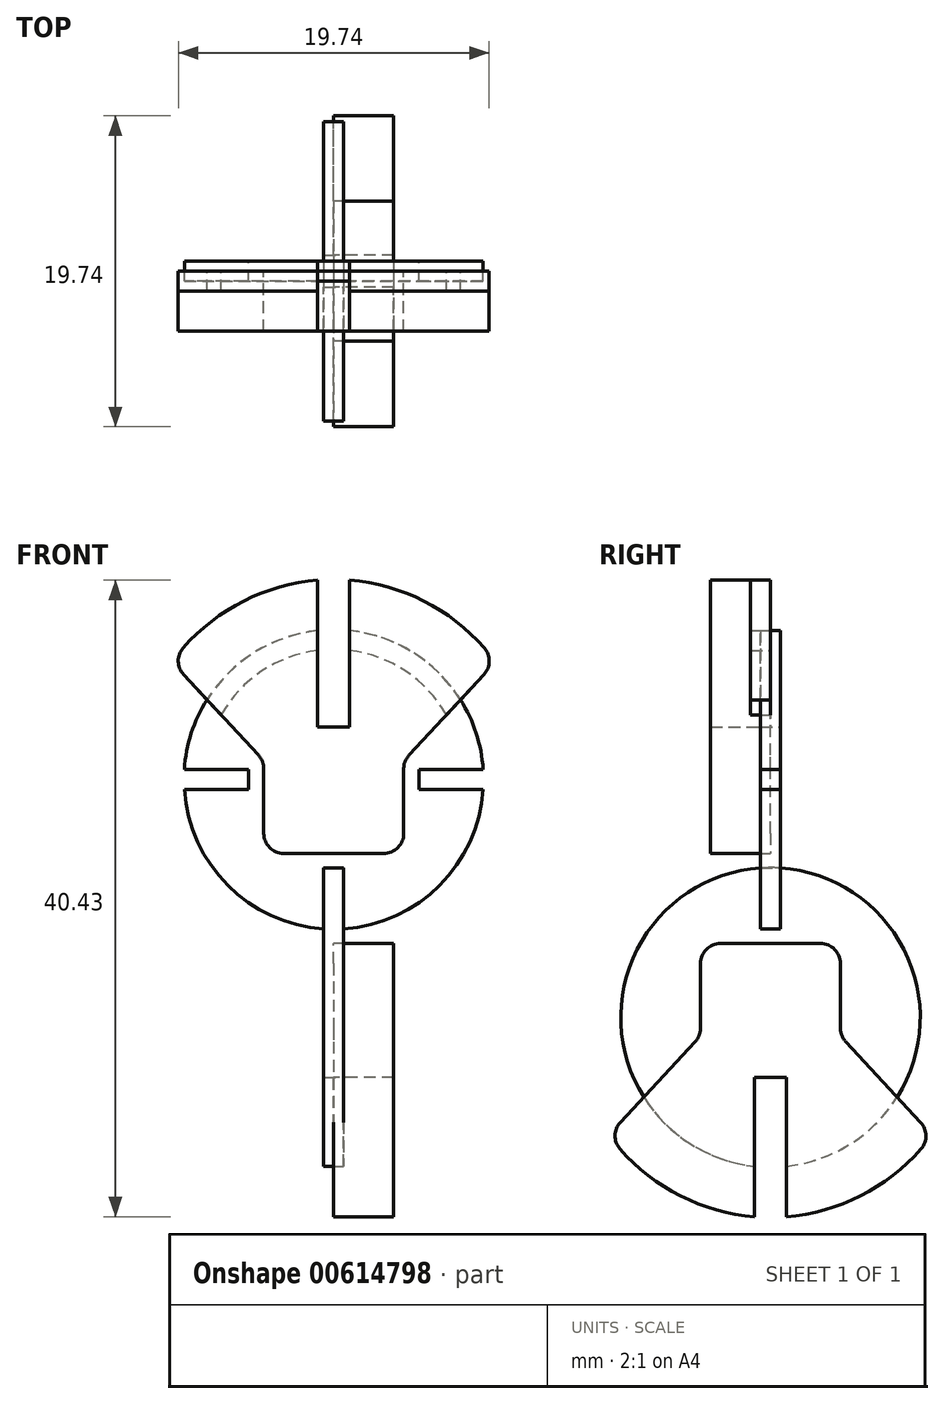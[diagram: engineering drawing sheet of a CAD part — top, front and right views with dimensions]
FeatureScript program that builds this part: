
annotation { "Feature Type Name" : "Feature", "Feature Type Description" : "" }
export const myFeature = defineFeature(function(context is Context, id is Id, definition is map)
    precondition{}
    {
        {
            var Q0;
            Q0=qCreatedBy(makeId("Front.planeOp"),FACE);
            var sketch = newSketch(context, id + "F0", { "sketchPlane" : qUnion([Q0])});
            skArc(sketch, "E0", {"start": v(-1.02, 9.46) * mm, "mid": v(0, -9.51) * mm, "end": v(1.02, 9.46) * mm});
            skLineSegment(sketch, "E1.bottom", {"start": v(0.63, -24.51) * mm, "end": v(-0.63, -24.51) * mm});
            skLineSegment(sketch, "E1.top", {"start": v(0.63, 24.51) * mm, "end": v(-0.63, 24.51) * mm});
            skLineSegment(sketch, "E1.left", {"start": v(0.64, -24.51) * mm, "end": v(0.64, -5.62) * mm});
            skLineSegment(sketch, "E1.right", {"start": v(-0.63, -24.51) * mm, "end": v(-0.63, -5.62) * mm});
            skLineSegment(sketch, "E2.bottom", {"start": v(0.64, 5.62) * mm, "end": v(-0.64, 5.62) * mm});
            skLineSegment(sketch, "E2.top", {"start": v(0.64, -5.62) * mm, "end": v(-0.64, -5.62) * mm});
            skLineSegment(sketch, "E3.trimOffspring", {"start": v(0.64, 5.62) * mm, "end": v(0.64, 24.51) * mm});
            skLineSegment(sketch, "E4.trimOffspring", {"start": v(-0.63, 5.62) * mm, "end": v(-0.63, 24.51) * mm});
            skPoint(sketch, "E5", {"position": v(0, 5.62) * mm});
            skLineSegment(sketch, "E6", {"start": v(-1.02, 9.46) * mm, "end": v(-1.02, 3.34) * mm});
            skLineSegment(sketch, "E7", {"start": v(1.02, 9.46) * mm, "end": v(1.02, 3.34) * mm});
            skLineSegment(sketch, "E8", {"start": v(-1.02, 3.34) * mm, "end": v(1.02, 3.34) * mm});
            skLineSegment(sketch, "E9", {"start": v(-1.02, 9.46) * mm, "end": v(-1.02, 12.66) * mm});
            skLineSegment(sketch, "E10", {"start": v(1.02, 9.46) * mm, "end": v(1.02, 12.66) * mm});
            skLineSegment(sketch, "E11.bottom", {"start": v(-5.43, -0.64) * mm, "end": v(-9.49, -0.64) * mm});
            skLineSegment(sketch, "E11.top", {"start": v(-5.43, 0.63) * mm, "end": v(-9.49, 0.63) * mm});
            skLineSegment(sketch, "E11.left", {"start": v(-5.43, -0.64) * mm, "end": v(-5.43, 0.63) * mm});
            skLineSegment(sketch, "E11.right", {"start": v(-9.49, -0.64) * mm, "end": v(-9.49, 0.63) * mm});
            skPoint(sketch, "E11.middle", {"position": v(-7.46, 0) * mm});
            skLineSegment(sketch, "E12", {"start": v(-3.18, -4.7) * mm, "end": v(3.18, -4.7) * mm});
            skLineSegment(sketch, "E13.MirrorCS", {"start": v(5.43, 0.63) * mm, "end": v(9.49, 0.63) * mm});
            skLineSegment(sketch, "E14.MirrorCS", {"start": v(5.43, -0.64) * mm, "end": v(9.49, -0.64) * mm});
            skLineSegment(sketch, "E15.MirrorCS", {"start": v(5.43, -0.64) * mm, "end": v(5.43, 0.63) * mm});
            skLineSegment(sketch, "E16", {"start": v(4.44, -3.42) * mm, "end": v(4.44, 0.68) * mm});
            skPoint(sketch, "E16.endSnap0", {"position": v(-7.46, 0.63) * mm});
            skLineSegment(sketch, "E17", {"start": v(4.78, 1.55) * mm, "end": v(9.53, 6.66) * mm});
            skLineSegment(sketch, "E18.MirrorCS", {"start": v(-4.44, -3.42) * mm, "end": v(-4.44, 0.68) * mm});
            skLineSegment(sketch, "E19.MirrorCS", {"start": v(-4.78, 1.55) * mm, "end": v(-9.53, 6.66) * mm});
            skArc(sketch, "E20.trimOffspring", {"start": v(7.16, 4.1) * mm, "mid": v(4.57, 6.87) * mm, "end": v(1.02, 8.2) * mm});
            skArc(sketch, "E21.trimOffspring", {"start": v(9.56, 8.36) * mm, "mid": v(5.7, 11.34) * mm, "end": v(1.02, 12.66) * mm});
            skArc(sketch, "E22.trimOffspring", {"start": v(-0.63, -8.23) * mm, "mid": v(0, -8.26) * mm, "end": v(0.64, -8.23) * mm});
            skArc(sketch, "E23.trimOffspring", {"start": v(-1.02, 8.2) * mm, "mid": v(-4.57, 6.87) * mm, "end": v(-7.16, 4.1) * mm});
            skPoint(sketch, "E24.visualSharp", {"position": v(-10.28, 7.46) * mm});
            skArc(sketch, "E24.filletArc", {"start": v(-9.56, 8.36) * mm, "mid": v(-9.87, 7.5) * mm, "end": v(-9.53, 6.66) * mm});
            skPoint(sketch, "E25.visualSharp", {"position": v(10.28, 7.46) * mm});
            skArc(sketch, "E25.filletArc", {"start": v(9.53, 6.66) * mm, "mid": v(9.87, 7.5) * mm, "end": v(9.56, 8.36) * mm});
            skPoint(sketch, "E26.visualSharp", {"position": v(4.44, 1.18) * mm});
            skArc(sketch, "E26.filletArc", {"start": v(4.78, 1.55) * mm, "mid": v(4.53, 1.15) * mm, "end": v(4.44, 0.68) * mm});
            skPoint(sketch, "E27.visualSharp", {"position": v(-4.44, 1.18) * mm});
            skArc(sketch, "E27.filletArc", {"start": v(-4.44, 0.68) * mm, "mid": v(-4.53, 1.15) * mm, "end": v(-4.78, 1.55) * mm});
            skPoint(sketch, "E28.visualSharp", {"position": v(-4.44, -4.7) * mm});
            skArc(sketch, "E28.filletArc", {"start": v(-4.44, -3.42) * mm, "mid": v(-4.07, -4.32) * mm, "end": v(-3.18, -4.7) * mm});
            skPoint(sketch, "E29.visualSharp", {"position": v(4.44, -4.7) * mm});
            skArc(sketch, "E29.filletArc", {"start": v(3.18, -4.7) * mm, "mid": v(4.07, -4.32) * mm, "end": v(4.44, -3.42) * mm});
            skArc(sketch, "E30.trimOffspring", {"start": v(-1.02, 12.66) * mm, "mid": v(-5.7, 11.34) * mm, "end": v(-9.56, 8.36) * mm});
            skSolve(sketch);
        }
        {
            var Q0;
            {var subQ6=sQuery(id+"F0.wireOp",EDGE,"E8");Q0=makeQuery(id+"F0.imprint","IMPRINT",FACE,{"disambiguationData":[TD([[makeQuery(id+"F0.imprint","IMPRINT",EDGE,{"derivedFrom":subQ6}),-1.0]])]});}
            var Q1;
            {var subQ5=sQuery(id+"F0.wireOp",EDGE,"E20.trimOffspring");Q1=makeQuery(id+"F0.imprint","IMPRINT",FACE,{"disambiguationData":[TD([[makeQuery(id+"F0.imprint","IMPRINT",EDGE,{"derivedFrom":subQ5}),-1.0]])]});}
            var Q2;
            {var subQ1=sQuery(id+"F0.wireOp",EDGE,"E10");Q2=makeQuery(id+"F0.imprint","IMPRINT",FACE,{"disambiguationData":[TD([[makeQuery(id+"F0.imprint","IMPRINT",EDGE,{"derivedFrom":subQ1}),-1.0]])]});}
            var Q3;
            {var subQ5=sQuery(id+"F0.wireOp",EDGE,"E23.trimOffspring");Q3=makeQuery(id+"F0.imprint","IMPRINT",FACE,{"disambiguationData":[TD([[makeQuery(id+"F0.imprint","IMPRINT",EDGE,{"derivedFrom":subQ5}),-1.0]])]});}
            var Q4;
            {var subQ1=sQuery(id+"F0.wireOp",EDGE,"E9");Q4=makeQuery(id+"F0.imprint","IMPRINT",FACE,{"disambiguationData":[TD([[makeQuery(id+"F0.imprint","IMPRINT",EDGE,{"derivedFrom":subQ1}),1.0]])]});}
            extrude(context, id + "F1", {"entities" : qUnion([Q0, Q1, Q2, Q3, Q4]), "depth" : 3.8 * mm, "offsetDistance" : 25.4 * mm});
        }
        {
            var Q0;
            {var subQ1=sQuery(id+"F0.wireOp",EDGE,"E9");Q0=makeQuery(id+"F0.imprint","IMPRINT",FACE,{"disambiguationData":[TD([[makeQuery(id+"F0.imprint","IMPRINT",EDGE,{"derivedFrom":subQ1}),1.0]])]});}
            var Q1;
            {var subQ5=sQuery(id+"F0.wireOp",EDGE,"E23.trimOffspring");Q1=makeQuery(id+"F0.imprint","IMPRINT",FACE,{"disambiguationData":[TD([[makeQuery(id+"F0.imprint","IMPRINT",EDGE,{"derivedFrom":subQ5}),-1.0]])]});}
            var Q2;
            {var subQ1=sQuery(id+"F0.wireOp",EDGE,"E10");Q2=makeQuery(id+"F0.imprint","IMPRINT",FACE,{"disambiguationData":[TD([[makeQuery(id+"F0.imprint","IMPRINT",EDGE,{"derivedFrom":subQ1}),-1.0]])]});}
            var Q3;
            {var subQ5=sQuery(id+"F0.wireOp",EDGE,"E20.trimOffspring");Q3=makeQuery(id+"F0.imprint","IMPRINT",FACE,{"disambiguationData":[TD([[makeQuery(id+"F0.imprint","IMPRINT",EDGE,{"derivedFrom":subQ5}),-1.0]])]});}
            extrude(context, id + "F2", {"entities" : qUnion([Q0, Q1, Q2, Q3]), "depth" : 3.17 * mm, "offsetDistance" : 25.4 * mm});
        }
        {
            var Q0;
            {var subQ4=sQuery(id+"F0.wireOp",EDGE,"E10");Q0=makeQuery(id+"F0.imprint","IMPRINT",FACE,{"disambiguationData":[TD([[makeQuery(id+"F0.imprint","IMPRINT",EDGE,{"derivedFrom":subQ4}),-1.0]])]});}
            var Q1;
            {var subQ1=sQuery(id+"F0.wireOp",EDGE,"E9");Q1=makeQuery(id+"F0.imprint","IMPRINT",FACE,{"disambiguationData":[TD([[makeQuery(id+"F0.imprint","IMPRINT",EDGE,{"derivedFrom":subQ1}),1.0]])]});}
            extrude(context, id + "F3", {"entities" : qUnion([Q0, Q1]), "depth" : 1.27 * mm, "offsetDistance" : 25.4 * mm});
        }
        {
            var Q0;
            Q0=makeQuery(id+"F2.opExtrude","SWEPT_BODY",BODY,{"disambiguationData":[OSD([sQuery(id+"F0.wireOp",EDGE,"E6"),sQuery(id+"F0.wireOp",EDGE,"E9"),sQuery(id+"F0.wireOp",EDGE,"E19.MirrorCS"),sQuery(id+"F0.wireOp",EDGE,"E23.trimOffspring"),sQuery(id+"F0.wireOp",EDGE,"E24.filletArc"),sQuery(id+"F0.wireOp",EDGE,"E30.trimOffspring")])]});
            var Q1;
            Q1=makeQuery(id+"F2.opExtrude","SWEPT_BODY",BODY,{"disambiguationData":[OSD([sQuery(id+"F0.wireOp",EDGE,"E7"),sQuery(id+"F0.wireOp",EDGE,"E10"),sQuery(id+"F0.wireOp",EDGE,"E17"),sQuery(id+"F0.wireOp",EDGE,"E20.trimOffspring"),sQuery(id+"F0.wireOp",EDGE,"E21.trimOffspring"),sQuery(id+"F0.wireOp",EDGE,"E25.filletArc")])]});
            deleteBodies(context, id + "F4", {"entities" : qUnion([Q0, Q1])});
        }
        {
            var Q0;
            {var subQ1=sQuery(id+"F0.wireOp",EDGE,"E9");Q0=makeQuery(id+"F0.imprint","IMPRINT",FACE,{"disambiguationData":[TD([[makeQuery(id+"F0.imprint","IMPRINT",EDGE,{"derivedFrom":subQ1}),1.0]])]});}
            var Q1;
            {var subQ5=sQuery(id+"F0.wireOp",EDGE,"E23.trimOffspring");Q1=makeQuery(id+"F0.imprint","IMPRINT",FACE,{"disambiguationData":[TD([[makeQuery(id+"F0.imprint","IMPRINT",EDGE,{"derivedFrom":subQ5}),-1.0]])]});}
            var Q2;
            {var subQ5=sQuery(id+"F0.wireOp",EDGE,"E20.trimOffspring");Q2=makeQuery(id+"F0.imprint","IMPRINT",FACE,{"disambiguationData":[TD([[makeQuery(id+"F0.imprint","IMPRINT",EDGE,{"derivedFrom":subQ5}),-1.0]])]});}
            var Q3;
            {var subQ4=sQuery(id+"F0.wireOp",EDGE,"E10");Q3=makeQuery(id+"F0.imprint","IMPRINT",FACE,{"disambiguationData":[TD([[makeQuery(id+"F0.imprint","IMPRINT",EDGE,{"derivedFrom":subQ4}),-1.0]])]});}
            extrude(context, id + "F5", {"entities" : qUnion([Q0, Q1, Q2, Q3]), "depth" : 1.27 * mm, "offsetDistance" : 25.4 * mm});
        }
        {
            var Q0;
            {var subQ5=sQuery(id+"F0.wireOp",EDGE,"E20.trimOffspring");Q0=makeQuery(id+"F0.imprint","IMPRINT",FACE,{"disambiguationData":[TD([[makeQuery(id+"F0.imprint","IMPRINT",EDGE,{"derivedFrom":subQ5}),-1.0]])]});}
            var Q1;
            {var subQ5=sQuery(id+"F0.wireOp",EDGE,"E23.trimOffspring");Q1=makeQuery(id+"F0.imprint","IMPRINT",FACE,{"disambiguationData":[TD([[makeQuery(id+"F0.imprint","IMPRINT",EDGE,{"derivedFrom":subQ5}),-1.0]])]});}
            var Q2;
            {var subQ6=sQuery(id+"F0.wireOp",EDGE,"E8");Q2=makeQuery(id+"F0.imprint","IMPRINT",FACE,{"disambiguationData":[TD([[makeQuery(id+"F0.imprint","IMPRINT",EDGE,{"derivedFrom":subQ6}),-1.0]])]});}
            var Q3;
            {var subQ12=sQuery(id+"F0.wireOp",EDGE,"E2.top");Q3=makeQuery(id+"F0.imprint","IMPRINT",FACE,{"disambiguationData":[TD([[makeQuery(id+"F0.imprint","IMPRINT",EDGE,{"derivedFrom":subQ12}),-1.0]])]});}
            extrude(context, id + "F6", {"entities" : qUnion([Q0, Q1, Q2, Q3]), "endBound" : BoundingType.SYMMETRIC, "depth" : 1.27 * mm, "offsetDistance" : 25.4 * mm});
        }
        {
            var Q0;
            Q0=qCreatedBy(makeId("Right.planeOp"),FACE);
            var sketch = newSketch(context, id + "F7", { "sketchPlane" : qUnion([Q0])});
            skArc(sketch, "E31", {"start": v(1.02, -24.57) * mm, "mid": v(0, -5.6) * mm, "end": v(-1.02, -24.57) * mm});
            skLineSegment(sketch, "E32.top", {"start": v(-0.64, -9.49) * mm, "end": v(0.64, -9.49) * mm});
            skLineSegment(sketch, "E33", {"start": v(1.02, -24.57) * mm, "end": v(1.02, -18.92) * mm});
            skLineSegment(sketch, "E34", {"start": v(-1.02, -24.57) * mm, "end": v(-1.02, -18.92) * mm});
            skLineSegment(sketch, "E35", {"start": v(1.02, -18.92) * mm, "end": v(-1.02, -18.92) * mm});
            skLineSegment(sketch, "E36", {"start": v(1.02, -24.57) * mm, "end": v(1.02, -27.77) * mm});
            skLineSegment(sketch, "E37", {"start": v(-1.02, -24.57) * mm, "end": v(-1.02, -27.77) * mm});
            skLineSegment(sketch, "E38", {"start": v(3.17, -10.42) * mm, "end": v(-3.18, -10.42) * mm});
            skLineSegment(sketch, "E39", {"start": v(-4.45, -11.69) * mm, "end": v(-4.45, -15.8) * mm});
            skLineSegment(sketch, "E40", {"start": v(-4.78, -16.66) * mm, "end": v(-9.53, -21.77) * mm});
            skLineSegment(sketch, "E41.MirrorCS", {"start": v(4.44, -11.69) * mm, "end": v(4.44, -15.8) * mm});
            skLineSegment(sketch, "E42.MirrorCS", {"start": v(4.78, -16.66) * mm, "end": v(9.53, -21.77) * mm});
            skArc(sketch, "E43.trimOffspring", {"start": v(-7.16, -19.22) * mm, "mid": v(-4.57, -21.99) * mm, "end": v(-1.02, -23.3) * mm});
            skArc(sketch, "E44.trimOffspring", {"start": v(-9.56, -23.47) * mm, "mid": v(-5.7, -26.46) * mm, "end": v(-1.02, -27.77) * mm});
            skArc(sketch, "E45.trimOffspring", {"start": v(1.02, -23.3) * mm, "mid": v(4.57, -21.99) * mm, "end": v(7.16, -19.22) * mm});
            skPoint(sketch, "E46.visualSharp", {"position": v(10.28, -22.57) * mm});
            skArc(sketch, "E46.filletArc", {"start": v(9.56, -23.47) * mm, "mid": v(9.87, -22.62) * mm, "end": v(9.53, -21.77) * mm});
            skPoint(sketch, "E47.visualSharp", {"position": v(-10.28, -22.57) * mm});
            skArc(sketch, "E47.filletArc", {"start": v(-9.53, -21.77) * mm, "mid": v(-9.87, -22.62) * mm, "end": v(-9.56, -23.47) * mm});
            skPoint(sketch, "E48.visualSharp", {"position": v(-4.45, -16.3) * mm});
            skArc(sketch, "E48.filletArc", {"start": v(-4.78, -16.66) * mm, "mid": v(-4.53, -16.26) * mm, "end": v(-4.44, -15.8) * mm});
            skPoint(sketch, "E49.visualSharp", {"position": v(4.44, -16.3) * mm});
            skArc(sketch, "E49.filletArc", {"start": v(4.44, -15.8) * mm, "mid": v(4.53, -16.26) * mm, "end": v(4.78, -16.66) * mm});
            skPoint(sketch, "E50.visualSharp", {"position": v(4.44, -10.42) * mm});
            skArc(sketch, "E50.filletArc", {"start": v(4.44, -11.69) * mm, "mid": v(4.07, -10.8) * mm, "end": v(3.17, -10.42) * mm});
            skPoint(sketch, "E51.visualSharp", {"position": v(-4.45, -10.42) * mm});
            skArc(sketch, "E51.filletArc", {"start": v(-3.18, -10.42) * mm, "mid": v(-4.07, -10.8) * mm, "end": v(-4.44, -11.69) * mm});
            skArc(sketch, "E52.trimOffspring", {"start": v(1.02, -27.77) * mm, "mid": v(5.7, -26.46) * mm, "end": v(9.56, -23.47) * mm});
            skSolve(sketch);
        }
        {
            var Q0;
            {var subQ6=sQuery(id+"F7.wireOp",EDGE,"E35");Q0=makeQuery(id+"F7.imprint","IMPRINT",FACE,{"disambiguationData":[TD([[makeQuery(id+"F7.imprint","IMPRINT",EDGE,{"derivedFrom":subQ6}),-1.0]])]});}
            var Q1;
            {var subQ5=sQuery(id+"F7.wireOp",EDGE,"E45.trimOffspring");Q1=makeQuery(id+"F7.imprint","IMPRINT",FACE,{"disambiguationData":[TD([[makeQuery(id+"F7.imprint","IMPRINT",EDGE,{"derivedFrom":subQ5}),-1.0]])]});}
            var Q2;
            {var subQ1=sQuery(id+"F7.wireOp",EDGE,"E36");Q2=makeQuery(id+"F7.imprint","IMPRINT",FACE,{"disambiguationData":[TD([[makeQuery(id+"F7.imprint","IMPRINT",EDGE,{"derivedFrom":subQ1}),1.0]])]});}
            var Q3;
            {var subQ5=sQuery(id+"F7.wireOp",EDGE,"E43.trimOffspring");Q3=makeQuery(id+"F7.imprint","IMPRINT",FACE,{"disambiguationData":[TD([[makeQuery(id+"F7.imprint","IMPRINT",EDGE,{"derivedFrom":subQ5}),-1.0]])]});}
            var Q4;
            {var subQ0=sQuery(id+"F7.wireOp",EDGE,"E37");Q4=makeQuery(id+"F7.imprint","IMPRINT",FACE,{"disambiguationData":[TD([[makeQuery(id+"F7.imprint","IMPRINT",EDGE,{"derivedFrom":subQ0}),-1.0]])]});}
            extrude(context, id + "F8", {"entities" : qUnion([Q0, Q1, Q2, Q3, Q4]), "depth" : 3.8 * mm, "offsetDistance" : 25.4 * mm});
        }
        {
            var Q0;
            Q0=makeQuery(id+"F7.imprint","IMPRINT",FACE,{"disambiguationData":[TD([[makeQuery(id+"F7.imprint","IMPRINT",EDGE,{"derivedFrom":sQuery(id+"F7.wireOp",EDGE,"E38")}),-1.0]])]});
            var Q1;
            {var subQ5=sQuery(id+"F7.wireOp",EDGE,"E43.trimOffspring");Q1=makeQuery(id+"F7.imprint","IMPRINT",FACE,{"disambiguationData":[TD([[makeQuery(id+"F7.imprint","IMPRINT",EDGE,{"derivedFrom":subQ5}),-1.0]])]});}
            var Q2;
            {var subQ6=sQuery(id+"F7.wireOp",EDGE,"E35");Q2=makeQuery(id+"F7.imprint","IMPRINT",FACE,{"disambiguationData":[TD([[makeQuery(id+"F7.imprint","IMPRINT",EDGE,{"derivedFrom":subQ6}),-1.0]])]});}
            var Q3;
            {var subQ5=sQuery(id+"F7.wireOp",EDGE,"E45.trimOffspring");Q3=makeQuery(id+"F7.imprint","IMPRINT",FACE,{"disambiguationData":[TD([[makeQuery(id+"F7.imprint","IMPRINT",EDGE,{"derivedFrom":subQ5}),-1.0]])]});}
            extrude(context, id + "F9", {"entities" : qUnion([Q0, Q1, Q2, Q3]), "endBound" : BoundingType.SYMMETRIC, "oppositeDirection" : true, "depth" : 1.27 * mm, "offsetDistance" : 25.4 * mm});
        }
    });
